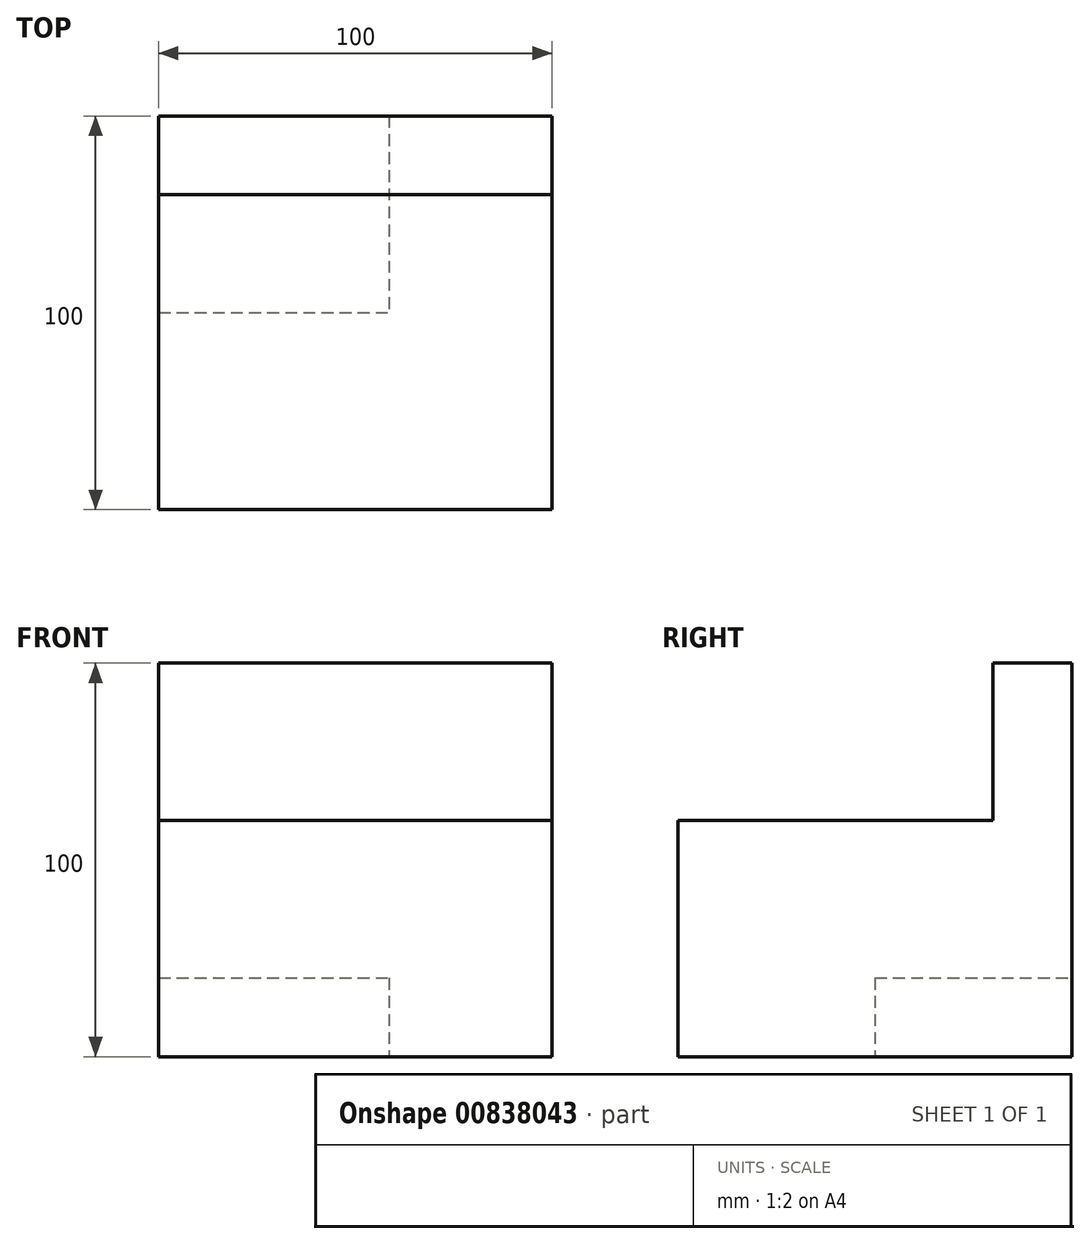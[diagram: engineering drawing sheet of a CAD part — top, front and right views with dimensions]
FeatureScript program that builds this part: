
annotation { "Feature Type Name" : "Feature", "Feature Type Description" : "" }
export const myFeature = defineFeature(function(context is Context, id is Id, definition is map)
    precondition{}
    {
        {
            var Q0;
            Q0=qCreatedBy(makeId("Top.planeOp"),FACE);
            var sketch = newSketch(context, id + "F0", { "sketchPlane" : qUnion([Q0])});
            skLineSegment(sketch, "E0.bottom", {"start": v(50, 50) * mm, "end": v(-50, 50) * mm});
            skLineSegment(sketch, "E0.top", {"start": v(50, -50) * mm, "end": v(-50, -50) * mm});
            skLineSegment(sketch, "E0.left", {"start": v(50, 50) * mm, "end": v(50, -50) * mm});
            skLineSegment(sketch, "E0.right", {"start": v(-50, 50) * mm, "end": v(-50, -50) * mm});
            skPoint(sketch, "E0.middle", {"position": v(0, 0) * mm});
            skSolve(sketch);
        }
        {
            var Q0;
            Q0 = qSketchRegion(id + "F0", true);
            extrude(context, id + "F1", {"entities" : qUnion([Q0]), "depth" : 100 * mm, "offsetDistance" : 25 * mm});
        }
        {
            var Q0;
            Q0=makeQuery(id+"F1.opExtrude","CAP_FACE",FACE,{"disambiguationData":[OSD([sQuery(id+"F0.wireOp",EDGE,"E0.bottom"),sQuery(id+"F0.wireOp",EDGE,"E0.top"),sQuery(id+"F0.wireOp",EDGE,"E0.left"),sQuery(id+"F0.wireOp",EDGE,"E0.right")])],"isStart":false});
            var sketch = newSketch(context, id + "F2", { "sketchPlane" : qUnion([Q0])});
            skLineSegment(sketch, "E1.bottom", {"start": v(-50, 30) * mm, "end": v(50, 30) * mm});
            skLineSegment(sketch, "E1.top", {"start": v(-50, -50) * mm, "end": v(50, -50) * mm});
            skLineSegment(sketch, "E1.left", {"start": v(-50, 30) * mm, "end": v(-50, -50) * mm});
            skLineSegment(sketch, "E1.right", {"start": v(50, 30) * mm, "end": v(50, -50) * mm});
            skSolve(sketch);
        }
        {
            var Q0;
            Q0 = qSketchRegion(id + "F2", true);
            extrude(context, id + "F3", {"entities" : qUnion([Q0]), "operationType" : NewBodyOperationType.REMOVE, "oppositeDirection" : true, "depth" : 40 * mm, "offsetDistance" : 25 * mm});
        }
        {
            var Q0;
            Q0=qCreatedBy(makeId("Front.planeOp"),FACE);
            var sketch = newSketch(context, id + "F4", { "sketchPlane" : qUnion([Q0])});
            skLineSegment(sketch, "E2.bottom", {"start": v(-51.42, 20) * mm, "end": v(8.58, 20) * mm});
            skLineSegment(sketch, "E2.top", {"start": v(-51.42, -20) * mm, "end": v(8.58, -20) * mm});
            skLineSegment(sketch, "E2.left", {"start": v(-51.42, 20) * mm, "end": v(-51.42, -20) * mm});
            skLineSegment(sketch, "E2.right", {"start": v(8.58, 20) * mm, "end": v(8.58, -20) * mm});
            skSolve(sketch);
        }
        {
            var Q0;
            Q0 = qSketchRegion(id + "F4", true);
            extrude(context, id + "F5", {"entities" : qUnion([Q0]), "operationType" : NewBodyOperationType.REMOVE, "endBound" : BoundingType.THROUGH_ALL, "oppositeDirection" : true, "depth" : 25 * mm, "offsetDistance" : 25 * mm});
        }
    });
